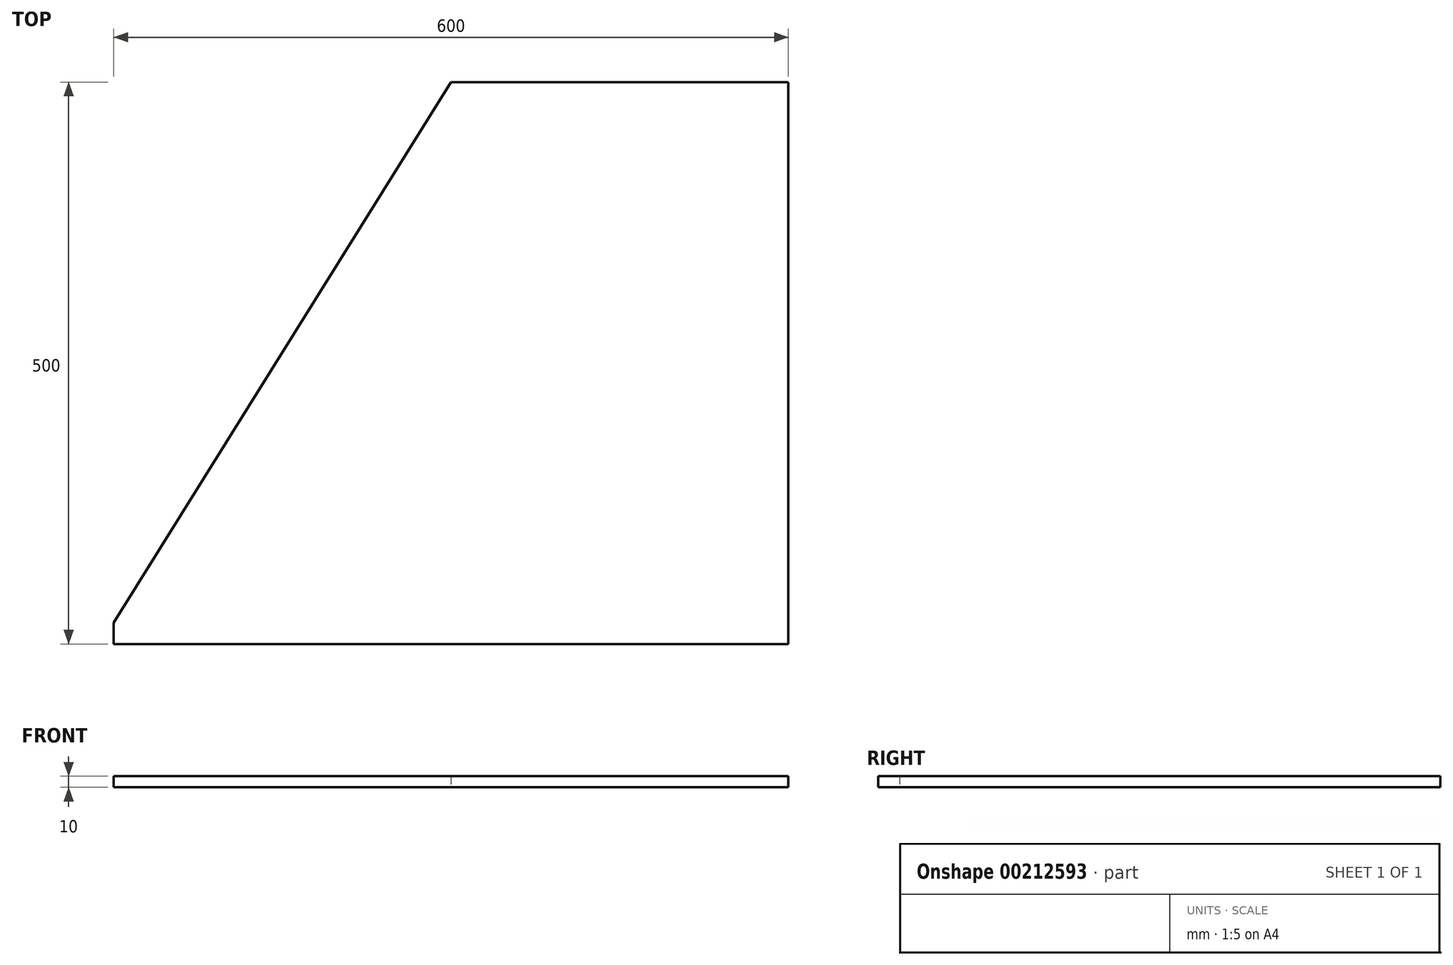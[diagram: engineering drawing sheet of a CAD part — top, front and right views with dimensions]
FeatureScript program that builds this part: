
annotation { "Feature Type Name" : "Feature", "Feature Type Description" : "" }
export const myFeature = defineFeature(function(context is Context, id is Id, definition is map)
    precondition{}
    {
        {
            var Q0;
            Q0=qCreatedBy(makeId("Top.planeOp"),FACE);
            var sketch = newSketch(context, id + "F0", { "sketchPlane" : qUnion([Q0])});
            skLineSegment(sketch, "E0", {"start": v(-300, -0.43) * mm, "end": v(-300, -19.43) * mm});
            skLineSegment(sketch, "E1", {"start": v(-300, -19.43) * mm, "end": v(300, -19.43) * mm});
            skLineSegment(sketch, "E2", {"start": v(300, -19.43) * mm, "end": v(300, 480.57) * mm});
            skLineSegment(sketch, "E3", {"start": v(300, 480.57) * mm, "end": v(0, 480.57) * mm});
            skLineSegment(sketch, "E4", {"start": v(0, 480.57) * mm, "end": v(-300, -0.43) * mm});
            skSolve(sketch);
        }
        {
            var Q0;
            Q0 = qSketchRegion(id + "F0", true);
            extrude(context, id + "F1", {"entities" : qUnion([Q0]), "depth" : 10 * mm});
        }
    });
